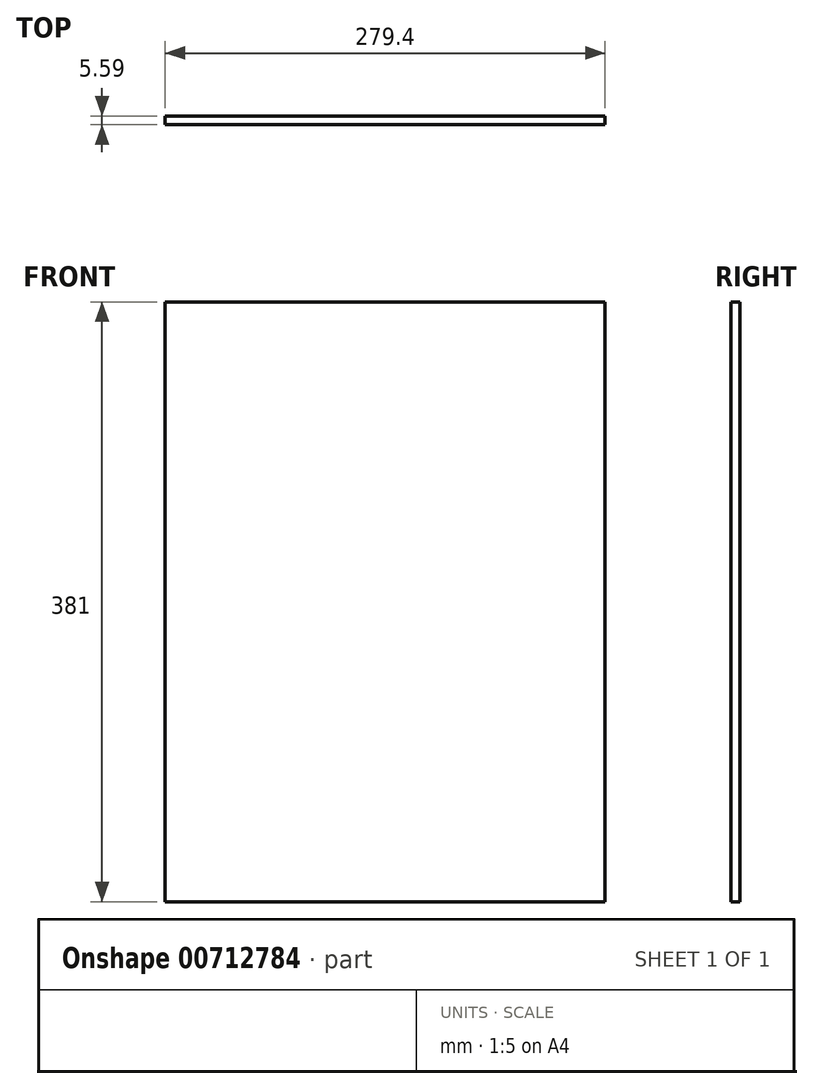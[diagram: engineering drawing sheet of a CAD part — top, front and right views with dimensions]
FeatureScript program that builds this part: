
annotation { "Feature Type Name" : "Feature", "Feature Type Description" : "" }
export const myFeature = defineFeature(function(context is Context, id is Id, definition is map)
    precondition{}
    {
        {
            var Q0;
            Q0=qCreatedBy(makeId("Front.planeOp"),FACE);
            var sketch = newSketch(context, id + "F0", { "sketchPlane" : qUnion([Q0])});
            skLineSegment(sketch, "E0.bottom", {"start": v(-291.56, 209.12) * mm, "end": v(-12.16, 209.12) * mm});
            skLineSegment(sketch, "E0.top", {"start": v(-291.56, -171.88) * mm, "end": v(-12.16, -171.88) * mm});
            skLineSegment(sketch, "E0.left", {"start": v(-291.56, 209.12) * mm, "end": v(-291.56, -171.88) * mm});
            skLineSegment(sketch, "E0.right", {"start": v(-12.16, 209.12) * mm, "end": v(-12.16, -171.88) * mm});
            skSolve(sketch);
        }
        {
            var Q0;
            Q0 = qSketchRegion(id + "F0", true);
            extrude(context, id + "F1", {"entities" : qUnion([Q0]), "depth" : 5.6 * mm, "offsetDistance" : 25.4 * mm});
        }
    });
